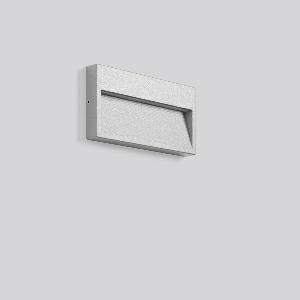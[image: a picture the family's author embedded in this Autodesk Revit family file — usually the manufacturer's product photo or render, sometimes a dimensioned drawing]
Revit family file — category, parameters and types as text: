
# Revit family: brick_duo_581634_004_1_3c87
name_source: partatom
category: Lighting Fixtures
units: mm (PartAtom-declared; Revit-internal decimal feet)

## family parameters
Cut with Voids When Loaded = No
Host = Face
Light Source = No
Part Type = Normal
Room Calculation Point = No
Round Connector Dimension = Use Diameter
Shared = No

## types (1)
- BRICK duo (1 x LED Modul 840, 180 lm, 4000)
    Apparent Load = 10 VA
    CIE Flux Codes = 49 80 95 96 100
    Color Rendering = 80
    Color Temperature = 4000
    Default Elevation = 1800 mm
    Description = Series: BRICK duo
Flat surface-mounted LED fitting for illumination of wall related areas such as stairs, ramps or corridors. Housing made of corrosion-resistant die-cast aluminium, powder-coated. Stainless steel screws. Diffuser with clear toughened glass. Asymmetrical downward light distribution for wide dispersion and uniform illumination. With compensation for drill hole deviations. Driver integrated. With connecting terminal up to 1 x 3 x 1.5 mm², for max. 13 mm diameter mains cable. 
Colour: silver, matt (approx. RAL 9006)
Length: 240 mm
Width: 120 mm
Height: 24 mm
Lamp: LED
System power: 10 W
Rated luminous flux: 180 lm
Luminous efficiency: 18 lm/W
Control gear: Regulated power supply
Protection class: I
Type of protection: IP 65
    Height = 24 mm  [stored 0.0787402 ft]
    Lamp = 1 x LED Modul 840
    Lamp Light Flux = 180 lm
    Lamp count = 1
    Length = 240 mm
    Lifetime = 50000 h
    Luminous efficacy = 18 lm/W
    Manufacturer = RZB
    ModVariant = No
    Model = 581634.004.1
    Mounting Place = Wall
    Mounting Type = Surface mounted
    Number of Poles = 1
    OnlyDefault = Yes
    Power Factor = 1
    Product Name = BRICK duo
    Product group = Surface mounted Wall luminaires
    ProductGroupID = 2001
    Protection Class = Protection class I
    Protection Degree = IP 65
    RLX_Detail_Level = 1
    RLX_Emergency_Light_Flux = 0 lm
    RLX_Emergency_Type = 0
    RLX_Emergency_Type_DB = No
    RlxData = <blob elided: 18873 chars, md5=13503826>
    Socket = socket
    Standby Power = 0 W
    System Light Flux = 180 lm
    System Power = 10 W
    Type Comments = Product without accessories
    Type Image = 581634.004.jpg
    URL = http://relux.com
    VarID = ---
    Voltage = 0 V
    Weight = 0.00 kg
    Width = 120 mm

note: [stored X ft] marks values corroborated as IEEE doubles in the binary element streams (Revit-internal decimal feet)

## geometry (parser evidence)
native form markers: Blend x4, Sweep x13
no freeform markers — native parametric forms only
